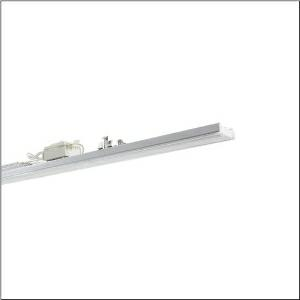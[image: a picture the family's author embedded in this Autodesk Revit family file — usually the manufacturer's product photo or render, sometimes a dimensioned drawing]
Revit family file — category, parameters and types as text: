
# Revit family: licross_r__11_recessed_mo_51tl12dn695g_08e0
name_source: partatom
category: Lighting Fixtures
units: mm (PartAtom-declared; Revit-internal decimal feet)

## family parameters
Cut with Voids When Loaded = No
Host = Face
Light Source = No
Part Type = Normal
Room Calculation Point = No
Round Connector Dimension = Use Diameter
Shared = No

## types (1)
- --- (1 x LED, 9990 lm, 56.7 W, 6500K)
    Apparent Load = 57 VA
    CIE Flux Codes = 67 92 99 100 100
    Color Rendering = 80
    Color Temperature = 6500K
    Default Elevation = 1800 mm
    Description = Licross® 11 Recessed MO, luminaire insert, of sheet steel, coil coated, white, length: 1.500mm, width: 66mm, height: 67mm, LED rated luminous flux: 9.990lm, light colour: 865, control gear: DALI 2, with plug, 5-pole, with phase selection, mains connection: 220..240V, AC, 50/60Hz, rated input power: 57W, internal wiring halogen-free, primary optical cover: cover, of PMMA, light emission: direct distribution, primary light characteristic: symmetric, protection rating (complete): IP40, insulation class (complete): insulation class I (protective earthing), certification: CE, ENEC, VDE, UKCA, protection symbol: D if used in an environment without relevant dust loads with corresponding accessories, impact resistance: IK06, permissible ambient temperature for indoor applications: -25..+35°C, corresponds to IFS (International Featured Standards) requirements for safety and quality in the food industry, reducing of maximum allowable ambient temperature of 5°C with ceiling mounting, LABS conformity tested according to VDMA 24364:2018-05, packaging unit: 1 piece
    Height = 58 mm
    Lamp = 1 x LED
    Lamp Light Flux = 9990 lm
    Lamp Power = 56.7 W
    Lamp count = 1
    Length = 1500 mm
    Luminous efficacy = 176 lm/W
    Manufacturer = Siteco
    ModVariant = No
    Model = 51TL12DN695G
    Mounting Place = Ceiling
    Mounting Type = Pendant
    Number of Poles = 1
    OnlyDefault = Yes
    Power Factor = 1
    Product Name = Licross® 11 Recessed MO
    Product group = luminaire insert | ceiling pendant
    ProductGroupID = 902
    Protection Class = Protection class I
    Protection Degree = IP 40
    RLX_Detail_Level = 1
    RLX_Emergency_Light_Flux = 0 lm
    RLX_Emergency_Type = 0
    RLX_Emergency_Type_DB = No
    RlxData = <blob elided: 24333 chars, md5=a64464df>
    Socket = socket
    Standby Power = 0 W
    System Light Flux = 9990 lm
    System Power = 57 W
    Type Comments = factory setting: luminous flux: 100 % | dim-lin: 254 | 378 mA
    Type Image = l_1296930.jpg
    URL = http://relux.com
    VarID = @adj_089261
    Voltage = 0 V
    Weight = 0.00 kg
    Width = 66 mm

## geometry (parser evidence)
native form markers: Blend x4, Sweep x9
no freeform markers — native parametric forms only
